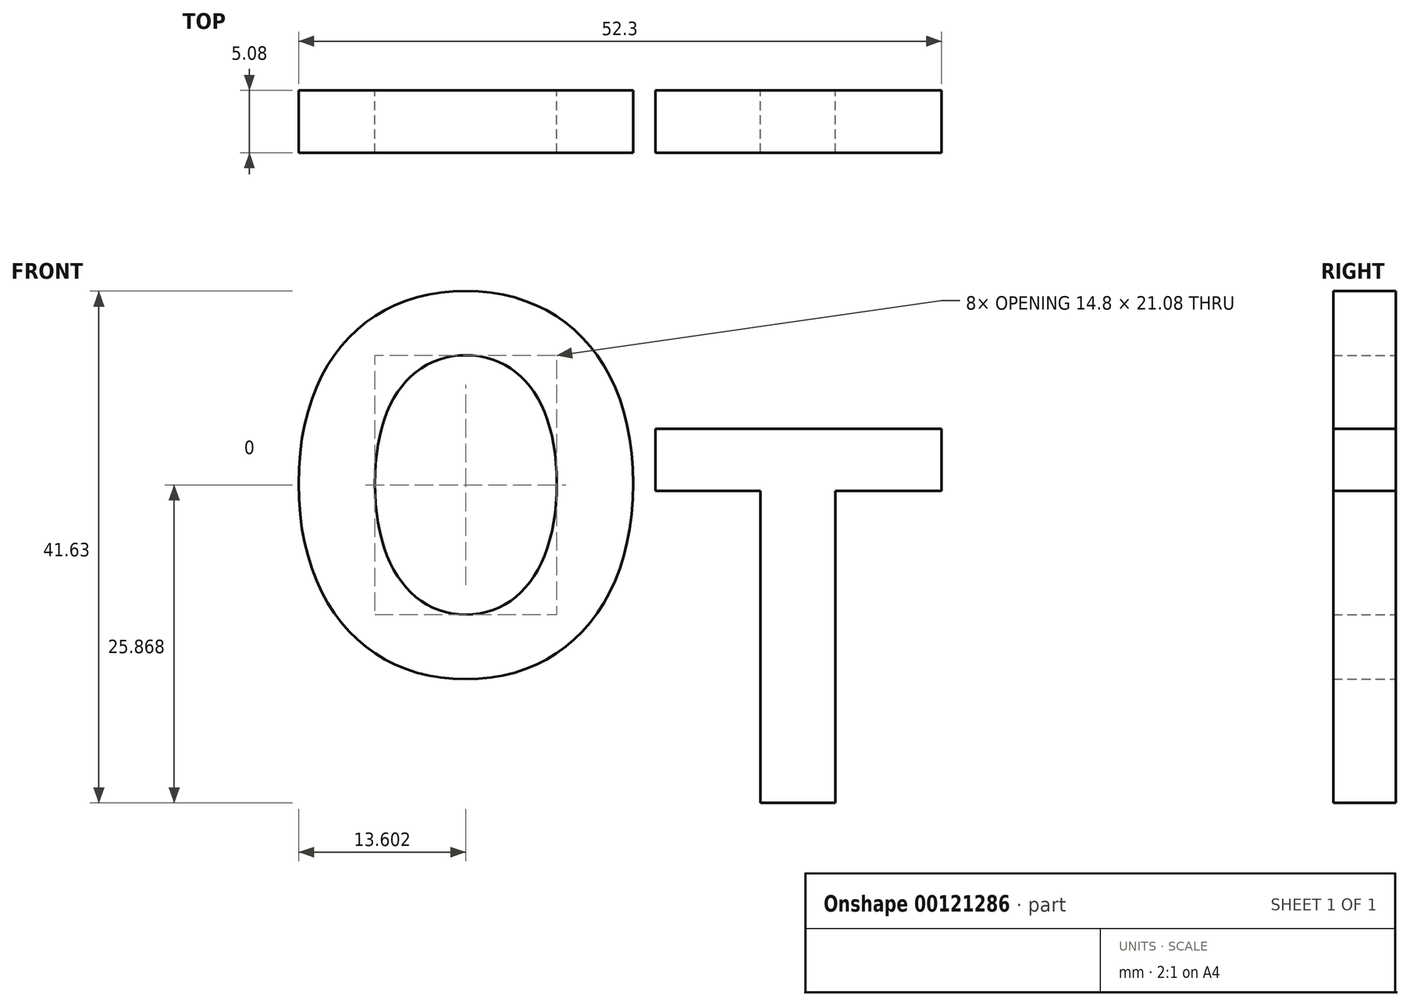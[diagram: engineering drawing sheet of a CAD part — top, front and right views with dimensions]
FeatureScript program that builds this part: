
annotation { "Feature Type Name" : "Feature", "Feature Type Description" : "" }
export const myFeature = defineFeature(function(context is Context, id is Id, definition is map)
    precondition{}
    {
        {
            var Q0;
            Q0=qCreatedBy(makeId("Front.planeOp"),FACE);
            var sketch = newSketch(context, id + "F0", { "sketchPlane" : qUnion([Q0])});
            skText(sketch, "E0", { "text": "O", "fontName": "NotoSansCJKsc-Bold.otf"});
            const initialGuessF0  = {"E0": [-0.04931, -0.0029, 1, 0, 0.02959]};
            skSetInitialGuess(sketch, initialGuessF0);
            skSolve(sketch);
        }
        {
            var Q0;
            Q0 = qSketchRegion(id + "F0", true);
            extrude(context, id + "F1", {"entities" : qUnion([Q0]), "depth" : 5.08 * mm});
        }
        {
            var Q0;
            Q0=qCreatedBy(makeId("Front.planeOp"),FACE);
            var sketch = newSketch(context, id + "F2", { "sketchPlane" : qUnion([Q0])});
            skText(sketch, "E1", { "text": "T", "fontName": "NotoSansCJKsc-Bold.otf"});
            const initialGuessF2  = {"E1": [-0.01929, -0.01354, 1, 0, 0.0296]};
            skSetInitialGuess(sketch, initialGuessF2);
            skSolve(sketch);
        }
        {
            var Q0;
            Q0 = qSketchRegion(id + "F2", true);
            extrude(context, id + "F3", {"entities" : qUnion([Q0]), "depth" : 5.08 * mm});
        }
    });
